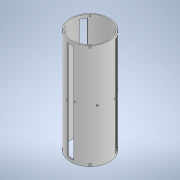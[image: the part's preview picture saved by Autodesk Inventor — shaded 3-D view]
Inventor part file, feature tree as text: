
AUTODESK INVENTOR PART (.ipt)
format: ipt  version: 2021 (Build 250183000, 183)  size: 261,120 bytes
history: native  units: in
note: dims shown in document units (in); Inventor stores cm internally (conversion verified against a paired STEP export)
features: other x26, plane x5, hole x5, pattern_circular x4, sketch x4, extrude x2
ambient origin geometry x8: Origin, YZ Plane, XZ Plane, XY Plane, X Axis, Y Axis, Z Axis, Center Point
bodies: Solid1 (feature_tree)
feature tree (46):
  extrude  "Extrusion1"  Depth=0.3937in
  plane  "Work Plane1"
  extrude  "Extrusion2"  Depth=0.3937in TaperAngle=0.0deg
  pattern_circular  "Circular Pattern1"  Count=3 Angle=360.0deg
  other  "Work Axis1"
  other  "Work Axis2"
  other  "Work Axis3"
  other  "Work Axis4"
  other  "Work Point1"
  other  "Work Point2"
  other  "Work Point3"
  other  "Central Plane"
  other  "Work Point4"
  other  "Work Axis6"
  other  "Work Axis7"
  other  "Offset Plane A"
  other  "Work Point5"
  other  "Work Point6"
  other  "Work Axis8"
  other  "Work Axis9"
  other  "Work Point7"
  other  "Work Point8"
  plane  "Work Plane5"
  plane  "Work Plane6"
  hole  "Hole1"  [1 undecoded]
  hole  "Hole2"  [1 undecoded]
  pattern_circular  "Circular Pattern3"  [2 undecoded]
  sketch  "Sketch5"  dims[d13=0.079in d14=-6.6929in]
  plane  "Work Plane7"
  sketch  "Sketch6"  dims[d15=0.079in d16=0.1574in d17=-0.1574in d48=1.0in d49=1.0in d29=0.096in d30=0.75in d31=0.185in d32=0.25in d33=0.5635in d34=1.0in d35=0.0in d52=1.0in d53=1.0in d38=0.096in d39=0.75in d40=0.185in d41=0.25in d42=0.5635in d43=1.0in d44=0.8108in d45=1.1811in d46=360.0deg d51=0.38in d54=0.177in d55=0.328in d56=0.332in d57=0.25in d58=0.5635in d59=0.484in d60=0.8108in d64=0.19in d65=0.177in d66=0.3229in d67=0.332in d68=0.25in d69=0.5635in d70=0.484in d71=0.8108in d72=1.5748in d73=360.0deg d75=60.0deg d76=1.0in d77=1.0in d78=0.129in d79=0.3229in d80=0.225in d81=0.25in d82=0.5635in d83=0.484in d84=0.8108in d85=1.1811in d86=360.0deg d61=0.75in d62=0.8108in d63=0.0625in]
  hole  "Hole3"  [1 undecoded]
  other  "Work Axis10"
  hole  "Hole4"  [1 undecoded]
  pattern_circular  "Circular Pattern5"  [2 undecoded]
  plane  "Work Plane12"
  hole  "Hole5"  [1 undecoded]
  pattern_circular  "Circular Pattern6"  Angle=60.0deg  [1 undecoded]
  sketch  "Sketch1"  dims[d3=0.0in d5=0.3937in]
  sketch  "Sketch2"  dims[d7=0.3937in d8=0.5in d9=0.0in d10=1.1811in d11=360.0deg]
  other  "Work Axis5"
  other  "Offset Plane B"
  other  "Work Axis11"
  other  "Work Axis12"
  other  "Work Point9"
  other  "Work Axis13"
  other  "Work Point10"
note: 10 required parameter values undecoded (feature->parameter linkage not recoverable at this tier; creation-order binding heuristic only, values carry confidence <= 0.55)
